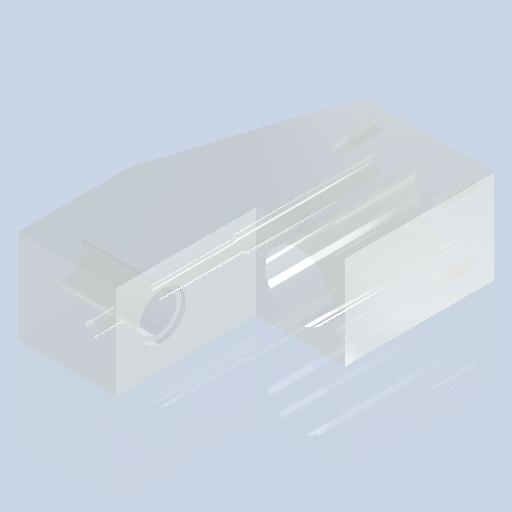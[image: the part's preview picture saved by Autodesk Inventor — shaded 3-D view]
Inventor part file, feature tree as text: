
AUTODESK INVENTOR PART (.ipt)
format: ipt  version: 2024.2 (Build 282272000, 272)  size: 350,208 bytes
history: native  units: mm
features: sketch x5, hole x4, plane x2, extrude x1, mirror x1, projected_geometry x1
ambient origin geometry x8: Origin, YZ Plane, XZ Plane, XY Plane, X Axis, Y Axis, Z Axis, Center Point
bodies: Volumenkörper1 (feature_tree)
feature tree (14):
  extrude  "Extrusion1"  Depth=21.0mm
  hole  "Bohrung2"  [1 undecoded]
  hole  "Bohrung3"  [1 undecoded]
  hole  "Bohrung4"  [1 undecoded]
  plane  "Arbeitsebene1"
  hole  "Bohrung7"  [1 undecoded]
  plane  "Arbeitsebene2"
  mirror  "Spiegeln2"
  sketch  "Skizze1"  dims[d0=62.0mm d1=21.0mm]
  sketch  "Skizze3"  dims[d2=30.0mm d3=38.0mm]
  sketch  "Skizze4"  dims[d4=28.0mm d5=12.0mm]
  sketch  "Skizze5"  dims[d6=20.0mm d7=0.0mm d16=10.0mm]
  sketch  "Skizze8"  dims[d17=14.0mm d18=6.0mm d19=4.0mm d20=2.0mm d21=90.0deg d22=8.0mm d23=20.594885mm d24=4.0mm d25=3.0mm d26=6.0mm d27=4.0mm d28=30.0mm d29=90.0deg d30=8.0mm d31=0.0mm d32=10.0mm d33=8.0mm d34=6.0mm d35=10.0mm d36=1.0mm d37=90.0deg d38=8.0mm d39=20.594885mm d49=12.0mm d57=14.0mm d58=2.459mm d59=6.0mm d60=4.0mm d61=2.0mm d62=90.0deg d63=9.0mm d64=20.594885mm d65=26.5mm]
  projected_geometry  "Projizierte Kontur1"
note: 4 required parameter values undecoded (feature->parameter linkage not recoverable at this tier; creation-order binding heuristic only, values carry confidence <= 0.55)
